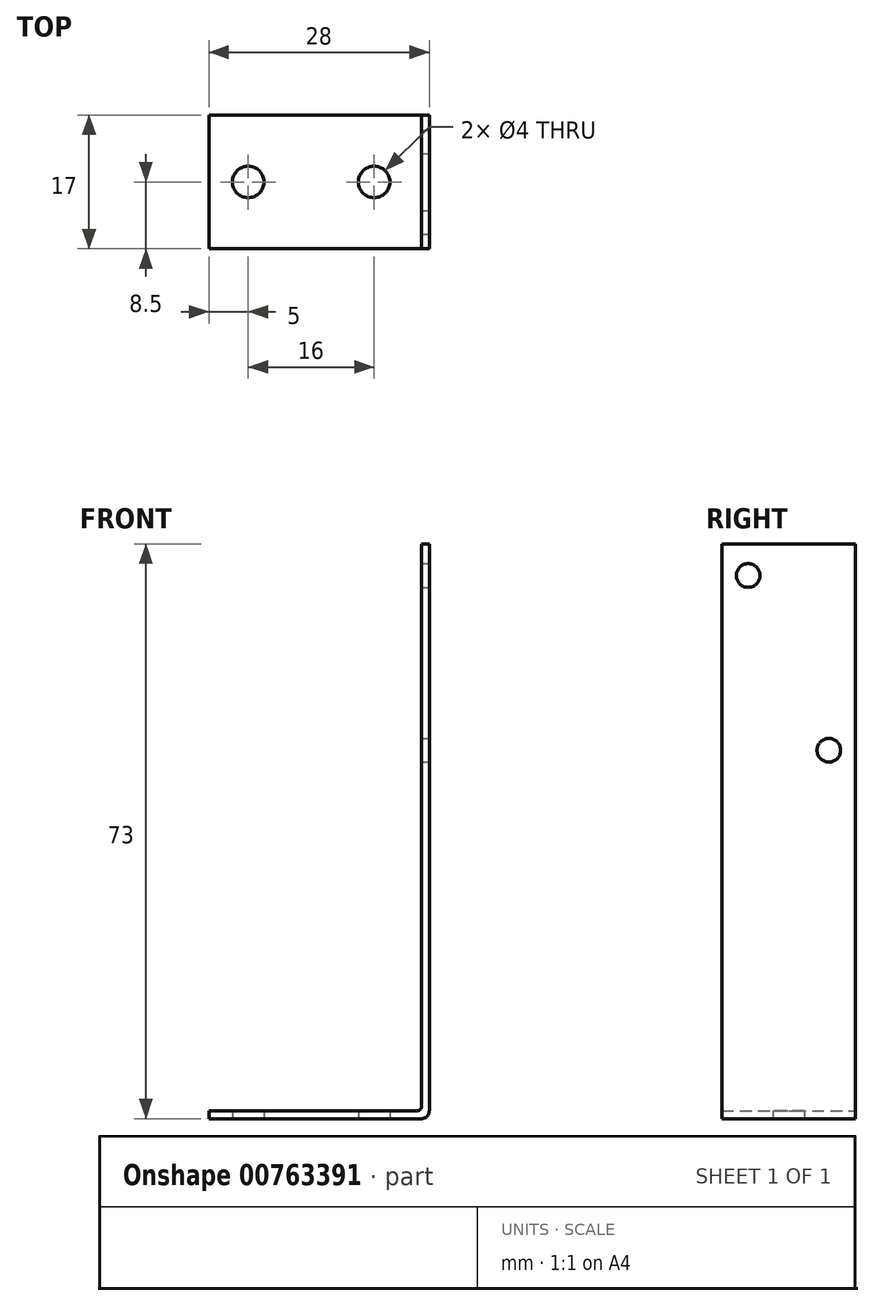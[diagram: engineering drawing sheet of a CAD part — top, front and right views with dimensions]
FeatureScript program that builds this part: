
annotation { "Feature Type Name" : "Feature", "Feature Type Description" : "" }
export const myFeature = defineFeature(function(context is Context, id is Id, definition is map)
    precondition{}
    {
        {
            var Q0;
            Q0=qCreatedBy(makeId("Front.planeOp"),FACE);
            var sketch = newSketch(context, id + "F0", { "sketchPlane" : qUnion([Q0])});
            skLineSegment(sketch, "E0", {"start": v(0, 73) * mm, "end": v(0, 0) * mm});
            skLineSegment(sketch, "E1", {"start": v(0, 0) * mm, "end": v(-28, 0) * mm});
            skLineSegment(sketch, "E2", {"start": v(0, 73) * mm, "end": v(-1, 73) * mm});
            skLineSegment(sketch, "E3", {"start": v(-1, 73) * mm, "end": v(-1, 1) * mm});
            skLineSegment(sketch, "E4", {"start": v(-1, 1) * mm, "end": v(-28, 1) * mm});
            skLineSegment(sketch, "E5", {"start": v(-28, 1) * mm, "end": v(-28, 0) * mm});
            skSolve(sketch);
        }
        {
            var Q0;
            Q0 = qSketchRegion(id + "F0", true);
            extrude(context, id + "F1", {"entities" : qUnion([Q0]), "endBound" : BoundingType.SYMMETRIC, "depth" : 17 * mm, "offsetDistance" : 25 * mm});
        }
        {
            var Q0;
            Q0=makeQuery(id+"F1.opExtrude","SWEPT_EDGE",EDGE,{"disambiguationData":[OSD([sQuery(id+"F0.wireOp",EDGE,"E0"),sQuery(id+"F0.wireOp",EDGE,"E1")])]});
            fillet(context, id + "F2", {"entities" : qUnion([Q0]), "radius" : 1 * mm, "tangentPropagation" : true, "allowEdgeOverflow" : false});
        }
        {
            var Q0;
            Q0=makeQuery(id+"F1.opExtrude","SWEPT_EDGE",EDGE,{"disambiguationData":[OSD([sQuery(id+"F0.wireOp",EDGE,"E3"),sQuery(id+"F0.wireOp",EDGE,"E4")])]});
            fillet(context, id + "F3", {"entities" : qUnion([Q0]), "radius" : 0.5 * mm, "tangentPropagation" : true, "allowEdgeOverflow" : false});
        }
        {
            var Q0;
            Q0=makeQuery(id+"F1.opExtrude","SWEPT_FACE",FACE,{"disambiguationData":[OSD([sQuery(id+"F0.wireOp",EDGE,"E1")])]});
            var sketch = newSketch(context, id + "F4", { "sketchPlane" : qUnion([Q0])});
            skCircle(sketch, "E6", {"center": v(-23, 0) * mm, "radius": 2 * mm});
            skCircle(sketch, "E7", {"center": v(-7, 0) * mm, "radius": 2 * mm});
            skSolve(sketch);
        }
        {
            var Q0;
            Q0 = qSketchRegion(id + "F4", true);
            extrude(context, id + "F5", {"entities" : qUnion([Q0]), "operationType" : NewBodyOperationType.REMOVE, "oppositeDirection" : true, "depth" : 3 * mm, "offsetDistance" : 25 * mm});
        }
        {
            var Q0;
            Q0=makeQuery(id+"F1.opExtrude","SWEPT_FACE",FACE,{"disambiguationData":[OSD([sQuery(id+"F0.wireOp",EDGE,"E0")])]});
            var sketch = newSketch(context, id + "F6", { "sketchPlane" : qUnion([Q0])});
            skCircle(sketch, "E8", {"center": v(5.1, 46.8) * mm, "radius": 1.5 * mm});
            skCircle(sketch, "E9", {"center": v(-5.15, 69) * mm, "radius": 1.5 * mm});
            skSolve(sketch);
        }
        {
            var Q0;
            Q0 = qSketchRegion(id + "F6", true);
            extrude(context, id + "F7", {"entities" : qUnion([Q0]), "operationType" : NewBodyOperationType.REMOVE, "oppositeDirection" : true, "depth" : 3 * mm, "offsetDistance" : 25 * mm});
        }
    });
